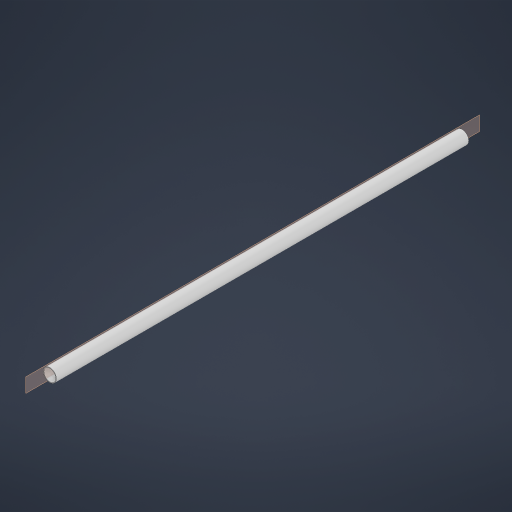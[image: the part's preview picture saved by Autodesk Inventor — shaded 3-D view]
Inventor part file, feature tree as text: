
AUTODESK INVENTOR PART (.ipt)
format: ipt  version: 2024 (Build 280153000, 153)  size: 188,928 bytes
history: native  units: mm
features: extrude x2, sketch x2, other x1, plane x1
ambient origin geometry x8: Origin, YZ Plane, XZ Plane, XY Plane, X Axis, Y Axis, Z Axis, Center Point
bodies: Body1 (feature_tree)
feature tree (6):
  other  "Sólido1"
  extrude  "Extrusión1"  Depth=170.62mm
  plane  "Plano de trabajo5"
  extrude  "Extrusión6"  [1 undecoded]
  sketch  "Boceto1"  dims[d0=190.0mm d1=170.62mm]
  sketch  "Boceto7"  dims[d2=6000.0mm d3=0.0mm d21=-47.5mm d22=105.0mm d23=100.0mm d24=0.0mm d7=0.5mm d8=0.872665mm d9=0.5mm d10=0.872665mm]
note: 1 required parameter value undecoded (feature->parameter linkage not recoverable at this tier; creation-order binding heuristic only, values carry confidence <= 0.55)
